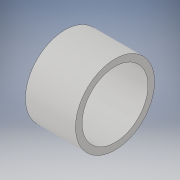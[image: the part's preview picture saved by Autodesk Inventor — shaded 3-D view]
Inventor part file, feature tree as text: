
AUTODESK INVENTOR PART (.ipt)
format: ipt  version: 2019 (Build 230136000, 136)  size: 99,328 bytes
history: native  units: mm
features: other x1, extrude x1, sketch x1
ambient origin geometry x8: Origin, YZ Plane, XZ Plane, XY Plane, X Axis, Y Axis, Z Axis, Center Point
bodies: Body1 (feature_tree)
feature tree (3):
  other  "Bryła1"
  extrude  "Wyciągnięcie proste1"  Depth=25.0mm
  sketch  "Szkic1"
